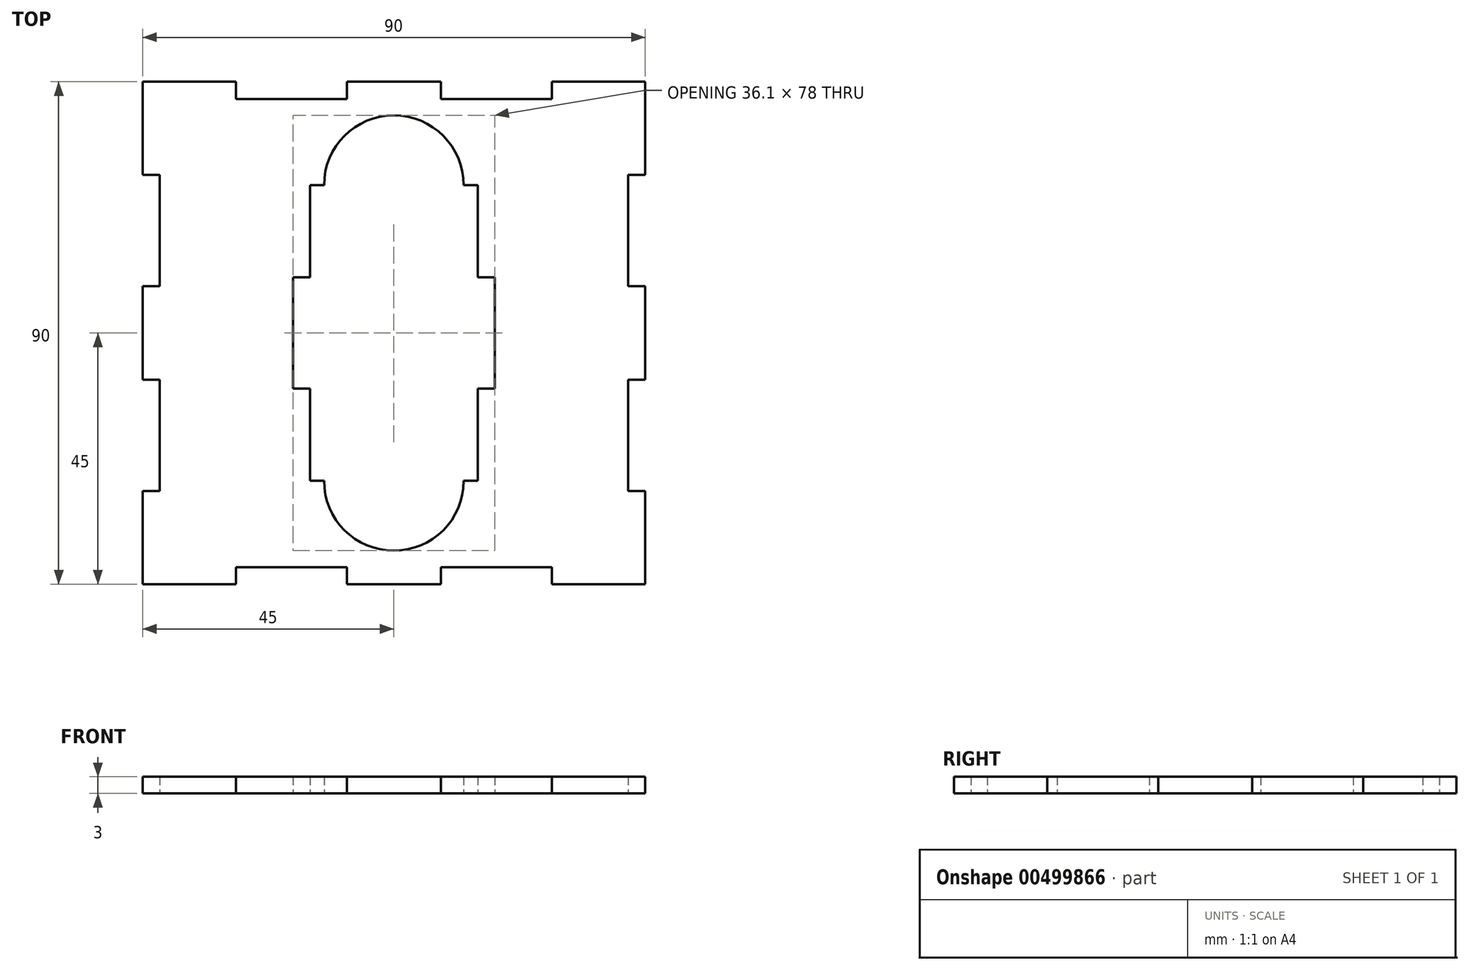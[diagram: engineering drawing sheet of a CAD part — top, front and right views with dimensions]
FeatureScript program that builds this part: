
annotation { "Feature Type Name" : "Feature", "Feature Type Description" : "" }
export const myFeature = defineFeature(function(context is Context, id is Id, definition is map)
    precondition{}
    {
        {
            var Q0;
            Q0=qCreatedBy(makeId("Top.planeOp"),FACE);
            var sketch = newSketch(context, id + "F0", { "sketchPlane" : qUnion([Q0])});
            skLineSegment(sketch, "E0.bottom", {"start": v(45, -45) * mm, "end": v(-45, -45) * mm});
            skLineSegment(sketch, "E0.top", {"start": v(45, 45) * mm, "end": v(-45, 45) * mm});
            skLineSegment(sketch, "E0.left", {"start": v(45, -45) * mm, "end": v(45, 45) * mm});
            skLineSegment(sketch, "E0.right", {"start": v(-45, -45) * mm, "end": v(-45, 45) * mm});
            skPoint(sketch, "E0.middle", {"position": v(0, 0) * mm});
            skLineSegment(sketch, "E1.bottom", {"start": v(15, -26.5) * mm, "end": v(-15, -26.5) * mm});
            skLineSegment(sketch, "E1.top", {"start": v(15, 26.5) * mm, "end": v(-15, 26.5) * mm});
            skLineSegment(sketch, "E1.left", {"start": v(15, -26.5) * mm, "end": v(15, 26.5) * mm});
            skLineSegment(sketch, "E1.right", {"start": v(-15, -26.5) * mm, "end": v(-15, 26.5) * mm});
            skCircle(sketch, "E2", {"center": v(0, 26.5) * mm, "radius": 12.5 * mm});
            skCircle(sketch, "E3", {"center": v(0, -26.5) * mm, "radius": 12.5 * mm});
            skLineSegment(sketch, "E4.bottom", {"start": v(-8.4, 41.95) * mm, "end": v(-28.3, 41.95) * mm});
            skLineSegment(sketch, "E4.top", {"start": v(-8.4, 45) * mm, "end": v(-28.3, 45) * mm});
            skLineSegment(sketch, "E4.left", {"start": v(-8.4, 41.95) * mm, "end": v(-8.4, 45) * mm});
            skLineSegment(sketch, "E4.right", {"start": v(-28.3, 41.95) * mm, "end": v(-28.3, 45) * mm});
            skPoint(sketch, "E4.middle", {"position": v(-18.35, 43.47) * mm});
            skLineSegment(sketch, "E5.bottom", {"start": v(28.3, 41.95) * mm, "end": v(8.4, 41.95) * mm});
            skLineSegment(sketch, "E5.top", {"start": v(28.3, 45) * mm, "end": v(8.4, 45) * mm});
            skLineSegment(sketch, "E5.left", {"start": v(28.3, 41.95) * mm, "end": v(28.3, 45) * mm});
            skLineSegment(sketch, "E5.right", {"start": v(8.4, 41.95) * mm, "end": v(8.4, 45) * mm});
            skPoint(sketch, "E5.middle", {"position": v(18.35, 43.48) * mm});
            skLineSegment(sketch, "E6.bottom", {"start": v(-41.95, 28.3) * mm, "end": v(-45, 28.3) * mm});
            skLineSegment(sketch, "E6.top", {"start": v(-41.95, 8.4) * mm, "end": v(-45, 8.4) * mm});
            skLineSegment(sketch, "E6.left", {"start": v(-41.95, 28.3) * mm, "end": v(-41.95, 8.4) * mm});
            skLineSegment(sketch, "E6.right", {"start": v(-45, 28.3) * mm, "end": v(-45, 8.4) * mm});
            skPoint(sketch, "E6.middle", {"position": v(-43.48, 18.35) * mm});
            skLineSegment(sketch, "E7.bottom", {"start": v(-41.95, -28.3) * mm, "end": v(-45, -28.3) * mm});
            skLineSegment(sketch, "E7.top", {"start": v(-41.95, -8.4) * mm, "end": v(-45, -8.4) * mm});
            skLineSegment(sketch, "E7.left", {"start": v(-41.95, -28.3) * mm, "end": v(-41.95, -8.4) * mm});
            skLineSegment(sketch, "E7.right", {"start": v(-45, -28.3) * mm, "end": v(-45, -8.4) * mm});
            skPoint(sketch, "E7.middle", {"position": v(-43.48, -18.35) * mm});
            skLineSegment(sketch, "E8.bottom", {"start": v(45, 8.4) * mm, "end": v(41.95, 8.4) * mm});
            skLineSegment(sketch, "E8.top", {"start": v(45, 28.3) * mm, "end": v(41.95, 28.3) * mm});
            skLineSegment(sketch, "E8.left", {"start": v(45, 8.4) * mm, "end": v(45, 28.3) * mm});
            skLineSegment(sketch, "E8.right", {"start": v(41.95, 8.4) * mm, "end": v(41.95, 28.3) * mm});
            skPoint(sketch, "E8.middle", {"position": v(43.48, 18.35) * mm});
            skLineSegment(sketch, "E9.bottom", {"start": v(45, -28.3) * mm, "end": v(41.95, -28.3) * mm});
            skLineSegment(sketch, "E9.top", {"start": v(45, -8.4) * mm, "end": v(41.95, -8.4) * mm});
            skLineSegment(sketch, "E9.left", {"start": v(45, -28.3) * mm, "end": v(45, -8.4) * mm});
            skLineSegment(sketch, "E9.right", {"start": v(41.95, -28.3) * mm, "end": v(41.95, -8.4) * mm});
            skPoint(sketch, "E9.middle", {"position": v(43.47, -18.35) * mm});
            skLineSegment(sketch, "E10.bottom", {"start": v(-8.4, -45) * mm, "end": v(-28.3, -45) * mm});
            skLineSegment(sketch, "E10.top", {"start": v(-8.4, -41.95) * mm, "end": v(-28.3, -41.95) * mm});
            skLineSegment(sketch, "E10.left", {"start": v(-8.4, -45) * mm, "end": v(-8.4, -41.95) * mm});
            skLineSegment(sketch, "E10.right", {"start": v(-28.3, -45) * mm, "end": v(-28.3, -41.95) * mm});
            skPoint(sketch, "E10.middle", {"position": v(-18.35, -43.48) * mm});
            skLineSegment(sketch, "E11.bottom", {"start": v(28.3, -45) * mm, "end": v(8.4, -45) * mm});
            skLineSegment(sketch, "E11.top", {"start": v(28.3, -41.95) * mm, "end": v(8.4, -41.95) * mm});
            skLineSegment(sketch, "E11.left", {"start": v(28.3, -45) * mm, "end": v(28.3, -41.95) * mm});
            skLineSegment(sketch, "E11.right", {"start": v(8.4, -45) * mm, "end": v(8.4, -41.95) * mm});
            skPoint(sketch, "E11.middle", {"position": v(18.35, -43.47) * mm});
            skLineSegment(sketch, "E12.bottom", {"start": v(-15, -9.95) * mm, "end": v(-18.05, -9.95) * mm});
            skLineSegment(sketch, "E12.top", {"start": v(-15, 9.95) * mm, "end": v(-18.05, 9.95) * mm});
            skLineSegment(sketch, "E12.left", {"start": v(-15, -9.95) * mm, "end": v(-15, 9.95) * mm});
            skLineSegment(sketch, "E12.right", {"start": v(-18.05, -9.95) * mm, "end": v(-18.05, 9.95) * mm});
            skPoint(sketch, "E12.middle", {"position": v(-16.53, 0) * mm});
            skLineSegment(sketch, "E13.bottom", {"start": v(18.05, -9.95) * mm, "end": v(15, -9.95) * mm});
            skLineSegment(sketch, "E13.top", {"start": v(18.05, 9.95) * mm, "end": v(15, 9.95) * mm});
            skLineSegment(sketch, "E13.left", {"start": v(18.05, -9.95) * mm, "end": v(18.05, 9.95) * mm});
            skLineSegment(sketch, "E13.right", {"start": v(15, -9.95) * mm, "end": v(15, 9.95) * mm});
            skPoint(sketch, "E13.middle", {"position": v(16.52, 0) * mm});
            skSolve(sketch);
        }
        {
            var Q0;
            {var subQ5=sQuery(id+"F0.wireOp",EDGE,"E1.left");Q0=makeQuery(id+"F0.imprint","IMPRINT",FACE,{"disambiguationData":[TD([[makeQuery(id+"F0.imprint","IMPRINT",EDGE,{"derivedFrom":subQ5}),-1.0]])]});}
            extrude(context, id + "F1", {"entities" : qUnion([Q0]), "depth" : 3 * mm});
        }
    });
